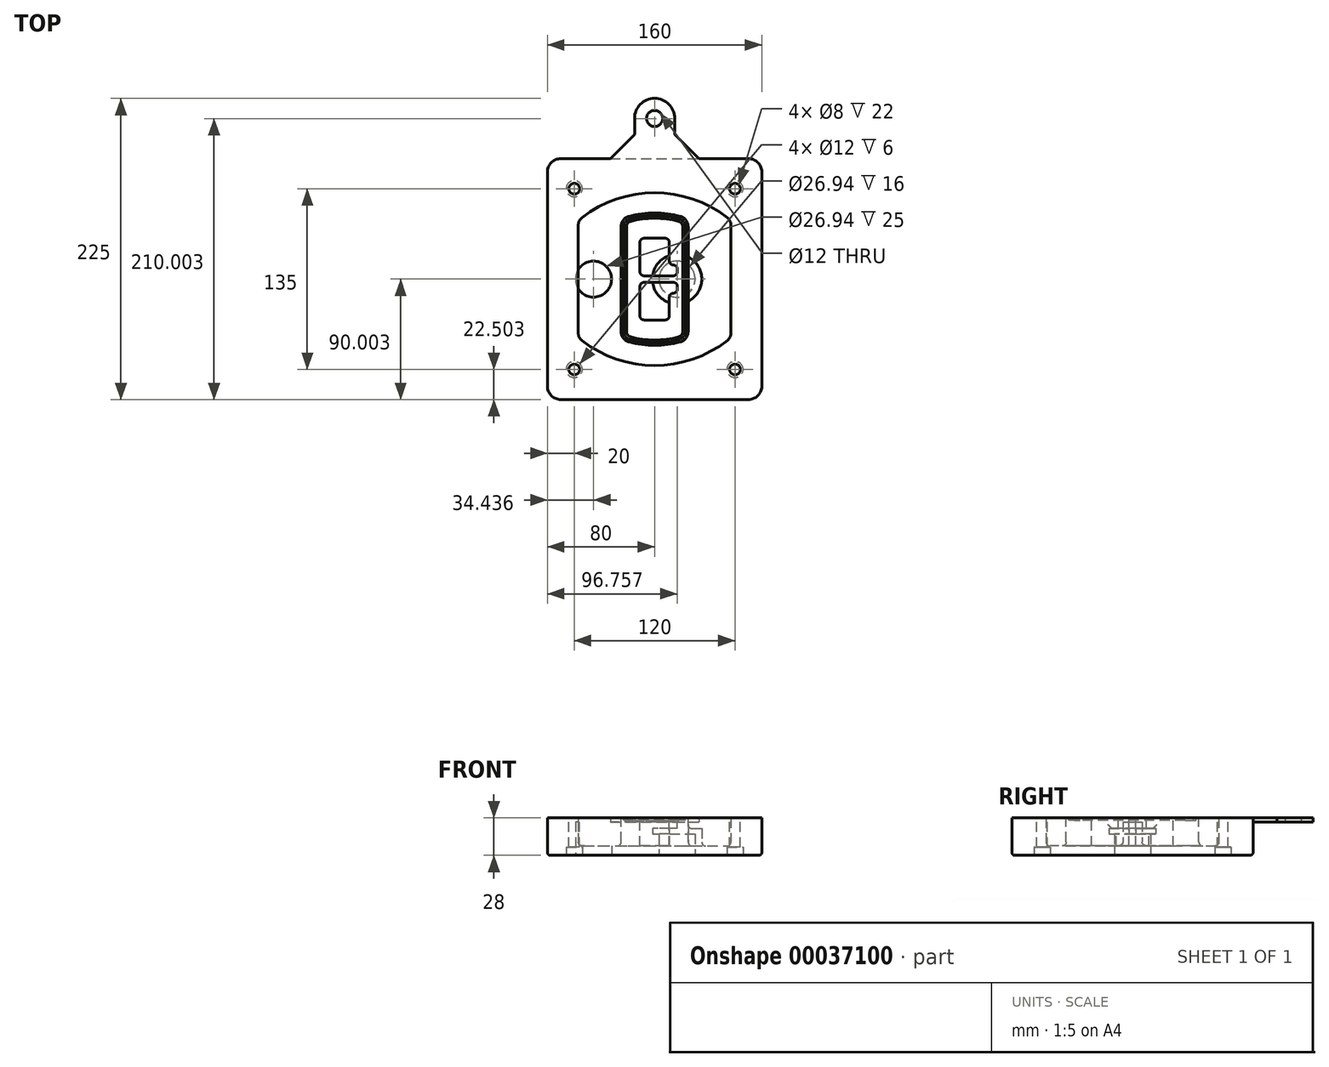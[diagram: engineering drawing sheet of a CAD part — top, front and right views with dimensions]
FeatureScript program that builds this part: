
annotation { "Feature Type Name" : "Feature", "Feature Type Description" : "" }
export const myFeature = defineFeature(function(context is Context, id is Id, definition is map)
    precondition{}
    {
        {
            var Q0;
            Q0=qCreatedBy(makeId("Top.planeOp"),FACE);
            var sketch = newSketch(context, id + "F0", { "sketchPlane" : qUnion([Q0])});
            skPoint(sketch, "E0.rect.middle", {"position": v(0, 0) * mm});
            skLineSegment(sketch, "E1.bottom", {"start": v(24.05, 28.38) * mm, "end": v(164.05, 28.38) * mm});
            skLineSegment(sketch, "E1.top", {"start": v(24.05, 208.38) * mm, "end": v(164.05, 208.38) * mm});
            skLineSegment(sketch, "E1.left", {"start": v(14.05, 38.38) * mm, "end": v(14.05, 198.38) * mm});
            skLineSegment(sketch, "E1.right", {"start": v(174.05, 38.38) * mm, "end": v(174.05, 198.38) * mm});
            skLineSegment(sketch, "E2", {"start": v(14.05, 208.38) * mm, "end": v(174.05, 28.38) * mm, "construction": true});
            skLineSegment(sketch, "E3", {"start": v(174.05, 208.38) * mm, "end": v(14.05, 28.38) * mm, "construction": true});
            skCircle(sketch, "E4", {"center": v(34.05, 185.88) * mm, "radius": 4 * mm});
            skCircle(sketch, "E5", {"center": v(154.05, 185.88) * mm, "radius": 4 * mm});
            skCircle(sketch, "E6", {"center": v(154.05, 50.88) * mm, "radius": 4 * mm});
            skCircle(sketch, "E7", {"center": v(34.05, 50.88) * mm, "radius": 4 * mm});
            skLineSegment(sketch, "E8", {"start": v(34.05, 185.88) * mm, "end": v(154.05, 185.88) * mm, "construction": true});
            skLineSegment(sketch, "E9", {"start": v(154.05, 185.88) * mm, "end": v(154.05, 50.88) * mm, "construction": true});
            skLineSegment(sketch, "E10", {"start": v(154.05, 50.88) * mm, "end": v(34.05, 50.88) * mm, "construction": true});
            skLineSegment(sketch, "E11", {"start": v(34.05, 50.88) * mm, "end": v(34.05, 185.88) * mm, "construction": true});
            skLineSegment(sketch, "E12", {"start": v(34.05, 158.68) * mm, "end": v(34.05, 78.09) * mm});
            skLineSegment(sketch, "E13", {"start": v(154.05, 158.68) * mm, "end": v(154.05, 78.09) * mm});
            skArc(sketch, "E14", {"start": v(150.2, 166.56) * mm, "mid": v(94.05, 185.88) * mm, "end": v(37.9, 166.56) * mm});
            skArc(sketch, "E15", {"start": v(37.9, 70.2) * mm, "mid": v(94.05, 50.88) * mm, "end": v(150.2, 70.2) * mm});
            skLineSegment(sketch, "E16", {"start": v(34.05, 118.38) * mm, "end": v(154.05, 118.38) * mm, "construction": true});
            skPoint(sketch, "E17.visualSharp", {"position": v(34.05, 73.38) * mm});
            skArc(sketch, "E17.filletArc", {"start": v(34.05, 78.09) * mm, "mid": v(35.06, 73.7) * mm, "end": v(37.9, 70.2) * mm});
            skPoint(sketch, "E18.visualSharp", {"position": v(34.05, 163.38) * mm});
            skArc(sketch, "E18.filletArc", {"start": v(37.9, 166.56) * mm, "mid": v(35.06, 163.06) * mm, "end": v(34.05, 158.68) * mm});
            skPoint(sketch, "E19.visualSharp", {"position": v(154.05, 163.38) * mm});
            skArc(sketch, "E19.filletArc", {"start": v(154.05, 158.68) * mm, "mid": v(153.04, 163.06) * mm, "end": v(150.2, 166.56) * mm});
            skPoint(sketch, "E20.visualSharp", {"position": v(154.05, 73.38) * mm});
            skArc(sketch, "E20.filletArc", {"start": v(150.2, 70.2) * mm, "mid": v(153.04, 73.7) * mm, "end": v(154.05, 78.09) * mm});
            skPoint(sketch, "E21.visualSharp", {"position": v(14.05, 208.38) * mm});
            skArc(sketch, "E21.filletArc", {"start": v(24.05, 208.38) * mm, "mid": v(16.98, 205.45) * mm, "end": v(14.05, 198.38) * mm});
            skPoint(sketch, "E22.visualSharp", {"position": v(174.05, 208.38) * mm});
            skArc(sketch, "E22.filletArc", {"start": v(174.05, 198.38) * mm, "mid": v(171.12, 205.45) * mm, "end": v(164.05, 208.38) * mm});
            skPoint(sketch, "E23.visualSharp", {"position": v(174.05, 28.38) * mm});
            skArc(sketch, "E23.filletArc", {"start": v(164.05, 28.38) * mm, "mid": v(171.12, 31.31) * mm, "end": v(174.05, 38.38) * mm});
            skPoint(sketch, "E24.visualSharp", {"position": v(14.05, 28.38) * mm});
            skArc(sketch, "E24.filletArc", {"start": v(14.05, 38.38) * mm, "mid": v(16.98, 31.31) * mm, "end": v(24.05, 28.38) * mm});
            skArc(sketch, "E25.0", {"start": v(151.05, 158.68) * mm, "mid": v(150.34, 161.75) * mm, "end": v(148.36, 164.2) * mm});
            skLineSegment(sketch, "E25.1", {"start": v(151.05, 158.68) * mm, "end": v(151.05, 78.09) * mm});
            skArc(sketch, "E25.2", {"start": v(148.36, 72.57) * mm, "mid": v(150.34, 75.02) * mm, "end": v(151.05, 78.09) * mm});
            skArc(sketch, "E25.3", {"start": v(39.74, 72.57) * mm, "mid": v(94.05, 53.88) * mm, "end": v(148.36, 72.57) * mm});
            skArc(sketch, "E25.4", {"start": v(37.05, 78.09) * mm, "mid": v(37.76, 75.02) * mm, "end": v(39.74, 72.57) * mm});
            skArc(sketch, "E25.5", {"start": v(148.36, 164.2) * mm, "mid": v(94.05, 182.88) * mm, "end": v(39.74, 164.2) * mm});
            skLineSegment(sketch, "E25.6", {"start": v(37.05, 158.68) * mm, "end": v(37.05, 78.09) * mm});
            skArc(sketch, "E25.7", {"start": v(39.74, 164.2) * mm, "mid": v(37.76, 161.75) * mm, "end": v(37.05, 158.68) * mm});
            skArc(sketch, "E26.0", {"start": v(35.43, 169.71) * mm, "mid": v(31.47, 164.82) * mm, "end": v(30.05, 158.68) * mm});
            skArc(sketch, "E26.1", {"start": v(152.67, 169.71) * mm, "mid": v(94.05, 189.88) * mm, "end": v(35.43, 169.71) * mm});
            skArc(sketch, "E26.2", {"start": v(158.05, 158.68) * mm, "mid": v(156.63, 164.82) * mm, "end": v(152.67, 169.71) * mm});
            skLineSegment(sketch, "E26.3", {"start": v(158.05, 158.68) * mm, "end": v(158.05, 78.09) * mm});
            skArc(sketch, "E26.4", {"start": v(152.67, 67.05) * mm, "mid": v(156.63, 71.95) * mm, "end": v(158.05, 78.09) * mm});
            skLineSegment(sketch, "E26.5", {"start": v(30.05, 158.68) * mm, "end": v(30.05, 78.09) * mm});
            skArc(sketch, "E26.6", {"start": v(35.43, 67.05) * mm, "mid": v(94.05, 46.88) * mm, "end": v(152.67, 67.05) * mm});
            skArc(sketch, "E26.7", {"start": v(30.05, 78.09) * mm, "mid": v(31.47, 71.95) * mm, "end": v(35.43, 67.05) * mm});
            skSolve(sketch);
        }
        {
            var Q0;
            Q0=makeQuery(id+"F0.imprint","IMPRINT",FACE,{"disambiguationData":[TD([[makeQuery(id+"F0.imprint","IMPRINT",EDGE,{"derivedFrom":sQuery(id+"F0.wireOp",EDGE,"E1.bottom")}),1.0]])]});
            var Q1;
            Q1=makeQuery(id+"F0.imprint","IMPRINT",FACE,{"disambiguationData":[TD([[makeQuery(id+"F0.imprint","IMPRINT",EDGE,{"derivedFrom":sQuery(id+"F0.wireOp",EDGE,"E12")}),1.0]])]});
            var Q2;
            Q2=makeQuery(id+"F0.imprint","IMPRINT",FACE,{"disambiguationData":[TD([[makeQuery(id+"F0.imprint","IMPRINT",EDGE,{"derivedFrom":sQuery(id+"F0.wireOp",EDGE,"E25.0")}),1.0]])]});
            var Q3;
            Q3=makeQuery(id+"F0.imprint","IMPRINT",FACE,{"disambiguationData":[TD([[makeQuery(id+"F0.imprint","IMPRINT",EDGE,{"derivedFrom":sQuery(id+"F0.wireOp",EDGE,"E12")}),-1.0]])]});
            extrude(context, id + "F1", {"entities" : qUnion([Q0, Q1, Q2, Q3]), "oppositeDirection" : true, "depth" : 25 * mm});
        }
        {
            var Q0;
            Q0=makeQuery(id+"F0.imprint","IMPRINT",FACE,{"disambiguationData":[TD([[makeQuery(id+"F0.imprint","IMPRINT",EDGE,{"derivedFrom":sQuery(id+"F0.wireOp",EDGE,"E12")}),1.0]])]});
            extrude(context, id + "F2", {"entities" : qUnion([Q0]), "operationType" : NewBodyOperationType.ADD, "depth" : 3 * mm});
        }
        {
            var Q0;
            Q0=makeQuery(id+"F0.imprint","IMPRINT",FACE,{"disambiguationData":[TD([[makeQuery(id+"F0.imprint","IMPRINT",EDGE,{"derivedFrom":sQuery(id+"F0.wireOp",EDGE,"E25.0")}),1.0]])]});
            extrude(context, id + "F3", {"entities" : qUnion([Q0]), "operationType" : NewBodyOperationType.REMOVE, "oppositeDirection" : true, "depth" : 18 * mm});
        }
        {
            var Q0;
            Q0=makeQuery(id+"F2.opExtrude","CAP_FACE",FACE,{"disambiguationData":[OSD([sQuery(id+"F0.wireOp",EDGE,"E12"),sQuery(id+"F0.wireOp",EDGE,"E13"),sQuery(id+"F0.wireOp",EDGE,"E14"),sQuery(id+"F0.wireOp",EDGE,"E15"),sQuery(id+"F0.wireOp",EDGE,"E17.filletArc"),sQuery(id+"F0.wireOp",EDGE,"E18.filletArc"),sQuery(id+"F0.wireOp",EDGE,"E19.filletArc"),sQuery(id+"F0.wireOp",EDGE,"E20.filletArc"),sQuery(id+"F0.wireOp",EDGE,"E25.0"),sQuery(id+"F0.wireOp",EDGE,"E25.1"),sQuery(id+"F0.wireOp",EDGE,"E25.2"),sQuery(id+"F0.wireOp",EDGE,"E25.3"),sQuery(id+"F0.wireOp",EDGE,"E25.4"),sQuery(id+"F0.wireOp",EDGE,"E25.5"),sQuery(id+"F0.wireOp",EDGE,"E25.6"),sQuery(id+"F0.wireOp",EDGE,"E25.7")])],"isStart":false});
            var sketch = newSketch(context, id + "F4", { "sketchPlane" : qUnion([Q0])});
            skArc(sketch, "E27.0", {"start": v(74.97, 71.41) * mm, "mid": v(94.05, 68.88) * mm, "end": v(113.13, 71.41) * mm});
            skArc(sketch, "E28.0", {"start": v(113.13, 165.35) * mm, "mid": v(94.05, 167.88) * mm, "end": v(74.97, 165.35) * mm});
            skLineSegment(sketch, "E29", {"start": v(69.05, 157.63) * mm, "end": v(69.05, 79.14) * mm});
            skLineSegment(sketch, "E30", {"start": v(119.05, 157.63) * mm, "end": v(119.05, 79.14) * mm});
            skLineSegment(sketch, "E31", {"start": v(69.05, 163.48) * mm, "end": v(119.05, 163.48) * mm, "construction": true});
            skLineSegment(sketch, "E32", {"start": v(69.05, 73.28) * mm, "end": v(119.05, 73.28) * mm, "construction": true});
            skPoint(sketch, "E33.visualSharp", {"position": v(69.05, 163.48) * mm});
            skArc(sketch, "E33.filletArc", {"start": v(74.97, 165.35) * mm, "mid": v(70.7, 162.5) * mm, "end": v(69.05, 157.63) * mm});
            skPoint(sketch, "E34.visualSharp", {"position": v(119.05, 163.48) * mm});
            skArc(sketch, "E34.filletArc", {"start": v(119.05, 157.63) * mm, "mid": v(117.4, 162.5) * mm, "end": v(113.13, 165.35) * mm});
            skPoint(sketch, "E35.visualSharp", {"position": v(119.05, 73.28) * mm});
            skArc(sketch, "E35.filletArc", {"start": v(113.13, 71.41) * mm, "mid": v(117.4, 74.27) * mm, "end": v(119.05, 79.14) * mm});
            skPoint(sketch, "E36.visualSharp", {"position": v(69.05, 73.28) * mm});
            skArc(sketch, "E36.filletArc", {"start": v(69.05, 79.14) * mm, "mid": v(70.7, 74.27) * mm, "end": v(74.97, 71.41) * mm});
            skArc(sketch, "E37.0", {"start": v(148.36, 164.2) * mm, "mid": v(94.05, 182.88) * mm, "end": v(39.74, 164.2) * mm});
            skArc(sketch, "E37.1", {"start": v(39.74, 164.2) * mm, "mid": v(37.76, 161.75) * mm, "end": v(37.05, 158.68) * mm});
            skLineSegment(sketch, "E37.2", {"start": v(37.05, 158.68) * mm, "end": v(37.05, 78.09) * mm});
            skArc(sketch, "E37.3", {"start": v(37.05, 78.09) * mm, "mid": v(37.76, 75.02) * mm, "end": v(39.74, 72.57) * mm});
            skArc(sketch, "E37.4", {"start": v(39.74, 72.57) * mm, "mid": v(94.05, 53.88) * mm, "end": v(148.36, 72.57) * mm});
            skArc(sketch, "E37.5", {"start": v(148.36, 72.57) * mm, "mid": v(150.34, 75.02) * mm, "end": v(151.05, 78.09) * mm});
            skLineSegment(sketch, "E37.6", {"start": v(151.05, 158.68) * mm, "end": v(151.05, 78.09) * mm});
            skArc(sketch, "E37.7", {"start": v(151.05, 158.68) * mm, "mid": v(150.34, 161.75) * mm, "end": v(148.36, 164.2) * mm});
            skLineSegment(sketch, "E38.0", {"start": v(117.05, 157.63) * mm, "end": v(117.05, 79.14) * mm});
            skArc(sketch, "E38.1", {"start": v(112.61, 73.34) * mm, "mid": v(115.81, 75.49) * mm, "end": v(117.05, 79.14) * mm});
            skArc(sketch, "E38.2", {"start": v(75.49, 73.34) * mm, "mid": v(94.05, 70.88) * mm, "end": v(112.61, 73.34) * mm});
            skArc(sketch, "E38.3", {"start": v(71.05, 79.14) * mm, "mid": v(72.29, 75.49) * mm, "end": v(75.49, 73.34) * mm});
            skLineSegment(sketch, "E38.4", {"start": v(71.05, 157.63) * mm, "end": v(71.05, 79.14) * mm});
            skArc(sketch, "E38.5", {"start": v(117.05, 157.63) * mm, "mid": v(115.81, 161.28) * mm, "end": v(112.61, 163.42) * mm});
            skArc(sketch, "E38.6", {"start": v(75.49, 163.42) * mm, "mid": v(72.29, 161.28) * mm, "end": v(71.05, 157.63) * mm});
            skArc(sketch, "E38.7", {"start": v(112.61, 163.42) * mm, "mid": v(94.05, 165.88) * mm, "end": v(75.49, 163.42) * mm});
            skArc(sketch, "E39.0", {"start": v(115.05, 157.63) * mm, "mid": v(114.23, 160.06) * mm, "end": v(112.1, 161.5) * mm});
            skLineSegment(sketch, "E39.1", {"start": v(115.05, 157.63) * mm, "end": v(115.05, 79.14) * mm});
            skArc(sketch, "E39.2", {"start": v(112.1, 75.27) * mm, "mid": v(114.23, 76.7) * mm, "end": v(115.05, 79.14) * mm});
            skArc(sketch, "E39.3", {"start": v(76, 75.27) * mm, "mid": v(94.05, 72.88) * mm, "end": v(112.1, 75.27) * mm});
            skArc(sketch, "E39.4", {"start": v(73.05, 79.14) * mm, "mid": v(73.87, 76.7) * mm, "end": v(76, 75.27) * mm});
            skArc(sketch, "E39.5", {"start": v(112.1, 161.5) * mm, "mid": v(94.05, 163.88) * mm, "end": v(76, 161.5) * mm});
            skLineSegment(sketch, "E39.6", {"start": v(73.05, 157.63) * mm, "end": v(73.05, 79.14) * mm});
            skArc(sketch, "E39.7", {"start": v(76, 161.5) * mm, "mid": v(73.87, 160.06) * mm, "end": v(73.05, 157.63) * mm});
            skLineSegment(sketch, "E40", {"start": v(69.05, 118.38) * mm, "end": v(119.05, 118.38) * mm, "construction": true});
            skLineSegment(sketch, "E41", {"start": v(83.05, 123.88) * mm, "end": v(83.05, 145.88) * mm});
            skLineSegment(sketch, "E42", {"start": v(86.05, 148.88) * mm, "end": v(102.05, 148.88) * mm});
            skLineSegment(sketch, "E43", {"start": v(105.05, 145.88) * mm, "end": v(105.05, 131.88) * mm});
            skLineSegment(sketch, "E44", {"start": v(108.05, 128.88) * mm, "end": v(108.05, 128.88) * mm});
            skLineSegment(sketch, "E45", {"start": v(111.05, 125.88) * mm, "end": v(111.05, 123.88) * mm});
            skLineSegment(sketch, "E46", {"start": v(108.05, 120.88) * mm, "end": v(86.05, 120.88) * mm});
            skPoint(sketch, "E47.visualSharp", {"position": v(83.05, 148.88) * mm});
            skArc(sketch, "E47.filletArc", {"start": v(86.05, 148.88) * mm, "mid": v(83.93, 148) * mm, "end": v(83.05, 145.88) * mm});
            skPoint(sketch, "E48.visualSharp", {"position": v(105.05, 148.88) * mm});
            skArc(sketch, "E48.filletArc", {"start": v(105.05, 145.88) * mm, "mid": v(104.17, 148) * mm, "end": v(102.05, 148.88) * mm});
            skPoint(sketch, "E49.visualSharp", {"position": v(105.05, 128.88) * mm});
            skArc(sketch, "E49.filletArc", {"start": v(105.05, 131.88) * mm, "mid": v(105.93, 129.76) * mm, "end": v(108.05, 128.88) * mm});
            skPoint(sketch, "E50.visualSharp", {"position": v(111.05, 128.88) * mm});
            skArc(sketch, "E50.filletArc", {"start": v(111.05, 125.88) * mm, "mid": v(110.17, 128) * mm, "end": v(108.05, 128.88) * mm});
            skPoint(sketch, "E51.visualSharp", {"position": v(111.05, 120.88) * mm});
            skArc(sketch, "E51.filletArc", {"start": v(108.05, 120.88) * mm, "mid": v(110.17, 121.76) * mm, "end": v(111.05, 123.88) * mm});
            skPoint(sketch, "E52.visualSharp", {"position": v(83.05, 120.88) * mm});
            skArc(sketch, "E52.filletArc", {"start": v(83.05, 123.88) * mm, "mid": v(83.93, 121.76) * mm, "end": v(86.05, 120.88) * mm});
            skLineSegment(sketch, "E53.0.MirrorCS", {"start": v(108.05, 115.88) * mm, "end": v(86.05, 115.88) * mm});
            skArc(sketch, "E54.0.MirrorCS", {"start": v(83.05, 112.88) * mm, "mid": v(83.93, 115) * mm, "end": v(86.05, 115.88) * mm});
            skLineSegment(sketch, "E55.0.MirrorCS", {"start": v(83.05, 112.88) * mm, "end": v(83.05, 90.88) * mm});
            skArc(sketch, "E56.0.MirrorCS", {"start": v(86.05, 87.88) * mm, "mid": v(83.93, 88.76) * mm, "end": v(83.05, 90.88) * mm});
            skLineSegment(sketch, "E57.0.MirrorCS", {"start": v(86.05, 87.88) * mm, "end": v(102.05, 87.88) * mm});
            skArc(sketch, "E58.0.MirrorCS", {"start": v(105.05, 90.88) * mm, "mid": v(104.17, 88.76) * mm, "end": v(102.05, 87.88) * mm});
            skLineSegment(sketch, "E59.0.MirrorCS", {"start": v(105.05, 90.88) * mm, "end": v(105.05, 104.88) * mm});
            skArc(sketch, "E60.0.MirrorCS", {"start": v(105.05, 104.88) * mm, "mid": v(105.93, 107) * mm, "end": v(108.05, 107.88) * mm});
            skArc(sketch, "E61.0.MirrorCS", {"start": v(111.05, 110.88) * mm, "mid": v(110.17, 108.76) * mm, "end": v(108.05, 107.88) * mm});
            skLineSegment(sketch, "E62.0.MirrorCS", {"start": v(111.05, 110.88) * mm, "end": v(111.05, 112.88) * mm});
            skArc(sketch, "E63.0.MirrorCS", {"start": v(108.05, 115.88) * mm, "mid": v(110.17, 115) * mm, "end": v(111.05, 112.88) * mm});
            skSolve(sketch);
        }
        {
            var Q0;
            Q0=makeQuery(id+"F4.imprint","IMPRINT",FACE,{"disambiguationData":[TD([[makeQuery(id+"F4.imprint","IMPRINT",EDGE,{"derivedFrom":sQuery(id+"F4.wireOp",EDGE,"E27.0")}),1.0]])]});
            var Q1;
            Q1=makeQuery(id+"F4.imprint","IMPRINT",FACE,{"disambiguationData":[TD([[makeQuery(id+"F4.imprint","IMPRINT",EDGE,{"derivedFrom":sQuery(id+"F4.wireOp",EDGE,"E38.0")}),-1.0]])]});
            var Q2;
            Q2=makeQuery(id+"F4.imprint","IMPRINT",FACE,{"disambiguationData":[TD([[makeQuery(id+"F4.imprint","IMPRINT",EDGE,{"derivedFrom":sQuery(id+"F4.wireOp",EDGE,"E39.0")}),1.0]])]});
            extrude(context, id + "F5", {"entities" : qUnion([Q0, Q1, Q2]), "operationType" : NewBodyOperationType.ADD, "endBound" : BoundingType.UP_TO_NEXT, "oppositeDirection" : true, "depth" : 25 * mm});
        }
        {
            var Q0;
            Q0=makeQuery(id+"F4.imprint","IMPRINT",FACE,{"disambiguationData":[TD([[makeQuery(id+"F4.imprint","IMPRINT",EDGE,{"derivedFrom":sQuery(id+"F4.wireOp",EDGE,"E38.0")}),-1.0]])]});
            extrude(context, id + "F6", {"entities" : qUnion([Q0]), "operationType" : NewBodyOperationType.REMOVE, "oppositeDirection" : true, "depth" : 2 * mm});
        }
        {
            var Q0;
            Q0=makeQuery(id+"F1.opExtrude","CAP_FACE",FACE,{"disambiguationData":[OSD([sQuery(id+"F0.wireOp",EDGE,"E1.bottom"),sQuery(id+"F0.wireOp",EDGE,"E1.top"),sQuery(id+"F0.wireOp",EDGE,"E1.left"),sQuery(id+"F0.wireOp",EDGE,"E1.right"),sQuery(id+"F0.wireOp",EDGE,"E4"),sQuery(id+"F0.wireOp",EDGE,"E5"),sQuery(id+"F0.wireOp",EDGE,"E6"),sQuery(id+"F0.wireOp",EDGE,"E7"),sQuery(id+"F0.wireOp",EDGE,"E21.filletArc"),sQuery(id+"F0.wireOp",EDGE,"E22.filletArc"),sQuery(id+"F0.wireOp",EDGE,"E23.filletArc"),sQuery(id+"F0.wireOp",EDGE,"E24.filletArc")])],"isStart":false});
            var sketch = newSketch(context, id + "F7", { "sketchPlane" : qUnion([Q0])});
            skCircle(sketch, "E64", {"center": v(110.8, -118.38) * mm, "radius": 13.47 * mm});
            skCircle(sketch, "E65", {"center": v(48.49, -118.38) * mm, "radius": 13.47 * mm});
            skLineSegment(sketch, "E66", {"start": v(174.05, -118.38) * mm, "end": v(14.05, -118.38) * mm});
            skCircle(sketch, "E67", {"center": v(110.8, -118.38) * mm, "radius": 18.47 * mm});
            skCircle(sketch, "E68", {"center": v(154.05, -185.88) * mm, "radius": 6 * mm});
            skCircle(sketch, "E69", {"center": v(34.05, -185.88) * mm, "radius": 6 * mm});
            skCircle(sketch, "E70", {"center": v(34.05, -50.88) * mm, "radius": 6 * mm});
            skCircle(sketch, "E71", {"center": v(154.05, -50.88) * mm, "radius": 6 * mm});
            skSolve(sketch);
        }
        {
            var Q0;
            {var subQ1=sQuery(id+"F7.wireOp",EDGE,"E66");var subQ4=sQuery(id+"F7.wireOp",EDGE,"E64");var subQ6=makeQuery(id+"F7.imprint","INTERSECT",VERTEX,{"disambiguationData":[OD(0.0)],"derivedFrom":[subQ4,subQ1]});Q0=makeQuery(id+"F7.imprint","IMPRINT",FACE,{"disambiguationData":[TD([[makeQuery(id+"F7.imprint","IMPRINT",EDGE,{"disambiguationData":[TD([[subQ6,-1.0]])],"derivedFrom":subQ4}),-1.0]])]});}
            var Q1;
            {var subQ0=sQuery(id+"F7.wireOp",EDGE,"E66");var subQ1=sQuery(id+"F7.wireOp",EDGE,"E64");var subQ3=makeQuery(id+"F7.imprint","INTERSECT",VERTEX,{"disambiguationData":[OD(0.0)],"derivedFrom":[subQ1,subQ0]});Q1=makeQuery(id+"F7.imprint","IMPRINT",FACE,{"disambiguationData":[TD([[makeQuery(id+"F7.imprint","IMPRINT",EDGE,{"disambiguationData":[TD([[subQ3,-1.0]])],"derivedFrom":subQ1}),1.0]])]});}
            var Q2;
            {var subQ0=sQuery(id+"F7.wireOp",EDGE,"E66");var subQ1=sQuery(id+"F7.wireOp",EDGE,"E64");var subQ3=makeQuery(id+"F7.imprint","INTERSECT",VERTEX,{"disambiguationData":[OD(0.0)],"derivedFrom":[subQ1,subQ0]});Q2=makeQuery(id+"F7.imprint","IMPRINT",FACE,{"disambiguationData":[TD([[makeQuery(id+"F7.imprint","IMPRINT",EDGE,{"disambiguationData":[TD([[subQ3,1.0]])],"derivedFrom":subQ1}),1.0]])]});}
            var Q3;
            {var subQ1=sQuery(id+"F7.wireOp",EDGE,"E66");var subQ4=sQuery(id+"F7.wireOp",EDGE,"E64");var subQ6=makeQuery(id+"F7.imprint","INTERSECT",VERTEX,{"disambiguationData":[OD(0.0)],"derivedFrom":[subQ4,subQ1]});Q3=makeQuery(id+"F7.imprint","IMPRINT",FACE,{"disambiguationData":[TD([[makeQuery(id+"F7.imprint","IMPRINT",EDGE,{"disambiguationData":[TD([[subQ6,1.0]])],"derivedFrom":subQ4}),-1.0]])]});}
            extrude(context, id + "F8", {"entities" : qUnion([Q0, Q1, Q2, Q3]), "operationType" : NewBodyOperationType.ADD, "oppositeDirection" : true, "depth" : 20 * mm});
        }
        {
            var Q0;
            {var subQ0=sQuery(id+"F7.wireOp",EDGE,"E66");var subQ1=sQuery(id+"F7.wireOp",EDGE,"E64");var subQ3=makeQuery(id+"F7.imprint","INTERSECT",VERTEX,{"disambiguationData":[OD(0.0)],"derivedFrom":[subQ1,subQ0]});Q0=makeQuery(id+"F7.imprint","IMPRINT",FACE,{"disambiguationData":[TD([[makeQuery(id+"F7.imprint","IMPRINT",EDGE,{"disambiguationData":[TD([[subQ3,-1.0]])],"derivedFrom":subQ1}),1.0]])]});}
            var Q1;
            {var subQ0=sQuery(id+"F7.wireOp",EDGE,"E66");var subQ1=sQuery(id+"F7.wireOp",EDGE,"E64");var subQ3=makeQuery(id+"F7.imprint","INTERSECT",VERTEX,{"disambiguationData":[OD(0.0)],"derivedFrom":[subQ1,subQ0]});Q1=makeQuery(id+"F7.imprint","IMPRINT",FACE,{"disambiguationData":[TD([[makeQuery(id+"F7.imprint","IMPRINT",EDGE,{"disambiguationData":[TD([[subQ3,1.0]])],"derivedFrom":subQ1}),1.0]])]});}
            extrude(context, id + "F9", {"entities" : qUnion([Q0, Q1]), "operationType" : NewBodyOperationType.REMOVE, "oppositeDirection" : true, "depth" : 16 * mm});
        }
        {
            var Q0;
            {var subQ0=sQuery(id+"F7.wireOp",EDGE,"E66");var subQ1=sQuery(id+"F7.wireOp",EDGE,"E65");var subQ3=makeQuery(id+"F7.imprint","INTERSECT",VERTEX,{"disambiguationData":[OD(0.0)],"derivedFrom":[subQ1,subQ0]});Q0=makeQuery(id+"F7.imprint","IMPRINT",FACE,{"disambiguationData":[TD([[makeQuery(id+"F7.imprint","IMPRINT",EDGE,{"disambiguationData":[TD([[subQ3,-1.0]])],"derivedFrom":subQ1}),1.0]])]});}
            var Q1;
            {var subQ0=sQuery(id+"F7.wireOp",EDGE,"E66");var subQ1=sQuery(id+"F7.wireOp",EDGE,"E65");var subQ3=makeQuery(id+"F7.imprint","INTERSECT",VERTEX,{"disambiguationData":[OD(0.0)],"derivedFrom":[subQ1,subQ0]});Q1=makeQuery(id+"F7.imprint","IMPRINT",FACE,{"disambiguationData":[TD([[makeQuery(id+"F7.imprint","IMPRINT",EDGE,{"disambiguationData":[TD([[subQ3,1.0]])],"derivedFrom":subQ1}),1.0]])]});}
            extrude(context, id + "F10", {"entities" : qUnion([Q0, Q1]), "operationType" : NewBodyOperationType.REMOVE, "oppositeDirection" : true, "depth" : 25 * mm});
        }
        {
            var Q0;
            Q0=makeQuery(id+"F7.imprint","IMPRINT",FACE,{"disambiguationData":[TD([[makeQuery(id+"F7.imprint","IMPRINT",EDGE,{"derivedFrom":sQuery(id+"F7.wireOp",EDGE,"E68")}),1.0]])]});
            var Q1;
            Q1=makeQuery(id+"F7.imprint","IMPRINT",FACE,{"disambiguationData":[TD([[makeQuery(id+"F7.imprint","IMPRINT",EDGE,{"derivedFrom":makeQuery(id+"F1.opExtrude","CAP_EDGE",EDGE,{"disambiguationData":[OSD([sQuery(id+"F0.wireOp",EDGE,"E5")])],"isStart":false})}),-1.0]])]});
            var Q2;
            Q2=makeQuery(id+"F7.imprint","IMPRINT",FACE,{"disambiguationData":[TD([[makeQuery(id+"F7.imprint","IMPRINT",EDGE,{"derivedFrom":sQuery(id+"F7.wireOp",EDGE,"E69")}),1.0]])]});
            var Q3;
            Q3=makeQuery(id+"F7.imprint","IMPRINT",FACE,{"disambiguationData":[TD([[makeQuery(id+"F7.imprint","IMPRINT",EDGE,{"derivedFrom":makeQuery(id+"F1.opExtrude","CAP_EDGE",EDGE,{"disambiguationData":[OSD([sQuery(id+"F0.wireOp",EDGE,"E4")])],"isStart":false})}),-1.0]])]});
            var Q4;
            Q4=makeQuery(id+"F7.imprint","IMPRINT",FACE,{"disambiguationData":[TD([[makeQuery(id+"F7.imprint","IMPRINT",EDGE,{"derivedFrom":sQuery(id+"F7.wireOp",EDGE,"E70")}),1.0]])]});
            var Q5;
            Q5=makeQuery(id+"F7.imprint","IMPRINT",FACE,{"disambiguationData":[TD([[makeQuery(id+"F7.imprint","IMPRINT",EDGE,{"derivedFrom":makeQuery(id+"F1.opExtrude","CAP_EDGE",EDGE,{"disambiguationData":[OSD([sQuery(id+"F0.wireOp",EDGE,"E7")])],"isStart":false})}),-1.0]])]});
            var Q6;
            Q6=makeQuery(id+"F7.imprint","IMPRINT",FACE,{"disambiguationData":[TD([[makeQuery(id+"F7.imprint","IMPRINT",EDGE,{"derivedFrom":sQuery(id+"F7.wireOp",EDGE,"E71")}),1.0]])]});
            var Q7;
            Q7=makeQuery(id+"F7.imprint","IMPRINT",FACE,{"disambiguationData":[TD([[makeQuery(id+"F7.imprint","IMPRINT",EDGE,{"derivedFrom":makeQuery(id+"F1.opExtrude","CAP_EDGE",EDGE,{"disambiguationData":[OSD([sQuery(id+"F0.wireOp",EDGE,"E6")])],"isStart":false})}),-1.0]])]});
            extrude(context, id + "F11", {"entities" : qUnion([Q0, Q1, Q2, Q3, Q4, Q5, Q6, Q7]), "operationType" : NewBodyOperationType.REMOVE, "oppositeDirection" : true, "depth" : 6 * mm});
        }
        {
            var Q0;
            Q0=makeQuery(id+"F9.boolean.opBoolean","COPY",FACE,{"derivedFrom":makeQuery(id+"F9.opExtrude","CAP_FACE",FACE,{"disambiguationData":[OSD([sQuery(id+"F7.wireOp",EDGE,"E64")])],"isStart":false})});
            var sketch = newSketch(context, id + "F12", { "sketchPlane" : qUnion([Q0])});
            skArc(sketch, "E72.0", {"start": v(105.05, -100.83) * mm, "mid": v(96.62, -106.56) * mm, "end": v(92.5, -115.88) * mm});
            skArc(sketch, "E72.1", {"start": v(92.5, -120.88) * mm, "mid": v(96.62, -130.2) * mm, "end": v(105.05, -135.93) * mm});
            skLineSegment(sketch, "E73", {"start": v(92.5, -120.88) * mm, "end": v(108.05, -120.88) * mm});
            skLineSegment(sketch, "E74.0", {"start": v(108.05, -115.88) * mm, "end": v(92.5, -115.88) * mm});
            skArc(sketch, "E74.1", {"start": v(108.05, -115.88) * mm, "mid": v(110.17, -115) * mm, "end": v(111.05, -112.88) * mm});
            skLineSegment(sketch, "E74.2", {"start": v(111.05, -110.88) * mm, "end": v(111.05, -112.88) * mm});
            skArc(sketch, "E74.3", {"start": v(111.05, -110.88) * mm, "mid": v(110.17, -108.76) * mm, "end": v(108.05, -107.88) * mm});
            skArc(sketch, "E74.4", {"start": v(105.05, -104.88) * mm, "mid": v(105.93, -107) * mm, "end": v(108.05, -107.88) * mm});
            skLineSegment(sketch, "E74.5", {"start": v(105.05, -100.83) * mm, "end": v(105.05, -104.88) * mm});
            skLineSegment(sketch, "E74.7", {"start": v(108.05, -120.88) * mm, "end": v(92.5, -120.88) * mm});
            skArc(sketch, "E74.8", {"start": v(108.05, -120.88) * mm, "mid": v(110.17, -121.76) * mm, "end": v(111.05, -123.88) * mm});
            skLineSegment(sketch, "E74.9", {"start": v(111.05, -125.88) * mm, "end": v(111.05, -123.88) * mm});
            skArc(sketch, "E74.10", {"start": v(111.05, -125.88) * mm, "mid": v(110.17, -128) * mm, "end": v(108.05, -128.88) * mm});
            skArc(sketch, "E74.11", {"start": v(105.05, -131.88) * mm, "mid": v(105.93, -129.76) * mm, "end": v(108.05, -128.88) * mm});
            skLineSegment(sketch, "E74.12", {"start": v(105.05, -135.93) * mm, "end": v(105.05, -131.88) * mm});
            skPoint(sketch, "E75.orphan", {"position": v(105.05, -145.88) * mm});
            skPoint(sketch, "E76.orphan", {"position": v(86.05, -120.88) * mm});
            skPoint(sketch, "E77.orphan", {"position": v(86.05, -115.88) * mm});
            skPoint(sketch, "E78.orphan", {"position": v(105.05, -90.88) * mm});
            skSolve(sketch);
        }
        {
            var Q0;
            {var subQ7=sQuery(id+"F12.wireOp",EDGE,"E72.0");var subQ14=sQuery(id+"F12.wireOp",EDGE,"E72.1");var subQ16=sQuery(id+"F12.wireOp",EDGE,"E74.1");var subQ18=sQuery(id+"F12.wireOp",EDGE,"E74.8");Q0=qUnion([makeQuery(id+"F12.imprint","IMPRINT",FACE,{"disambiguationData":[TD([[makeQuery(id+"F12.imprint","IMPRINT",EDGE,{"derivedFrom":subQ7}),1.0]])]}),makeQuery(id+"F12.imprint","IMPRINT",FACE,{"disambiguationData":[TD([[makeQuery(id+"F12.imprint","IMPRINT",EDGE,{"derivedFrom":subQ14}),1.0]])]}),makeQuery(id+"F12.imprint","IMPRINT",FACE,{"disambiguationData":[TD([[makeQuery(id+"F12.imprint","IMPRINT",EDGE,{"derivedFrom":subQ16}),1.0]])]}),makeQuery(id+"F12.imprint","IMPRINT",FACE,{"disambiguationData":[TD([[makeQuery(id+"F12.imprint","IMPRINT",EDGE,{"derivedFrom":subQ18}),-1.0]])]})]);}
            var Q1;
            Q1=makeQuery(id+"F5.boolean.opBoolean","SPLIT",FACE,{"disambiguationData":[TD([makeQuery(id+"F5.opExtrude","SWEPT_FACE",FACE,{"disambiguationData":[OSD([sQuery(id+"F4.wireOp",EDGE,"E41")])]})])],"derivedFrom":makeQuery(id+"F3.boolean.opBoolean","COPY",FACE,{"derivedFrom":makeQuery(id+"F3.opExtrude","CAP_FACE",FACE,{"disambiguationData":[OSD([sQuery(id+"F0.wireOp",EDGE,"E25.0"),sQuery(id+"F0.wireOp",EDGE,"E25.1"),sQuery(id+"F0.wireOp",EDGE,"E25.2"),sQuery(id+"F0.wireOp",EDGE,"E25.3"),sQuery(id+"F0.wireOp",EDGE,"E25.4"),sQuery(id+"F0.wireOp",EDGE,"E25.5"),sQuery(id+"F0.wireOp",EDGE,"E25.6"),sQuery(id+"F0.wireOp",EDGE,"E25.7")])],"isStart":false})})});
            extrude(context, id + "F13", {"entities" : qUnion([Q0]), "operationType" : NewBodyOperationType.REMOVE, "endBound" : BoundingType.UP_TO_SURFACE, "endBoundEntityFace" : qUnion([Q1]), "depth" : 25 * mm});
        }
        {
            var Q0;
            Q0=makeQuery(id+"F3.boolean.opBoolean","COPY",EDGE,{"derivedFrom":makeQuery(id+"F3.opExtrude","CAP_EDGE",EDGE,{"disambiguationData":[OSD([sQuery(id+"F0.wireOp",EDGE,"E25.6")])],"isStart":false})});
            var Q1;
            Q1=makeQuery(id+"F8.boolean.opBoolean","INTERSECT",EDGE,{"derivedFrom":[makeQuery(id+"F5.opExtrude","SWEPT_FACE",FACE,{"disambiguationData":[OSD([sQuery(id+"F4.wireOp",EDGE,"E30")])]}),makeQuery(id+"F8.opExtrude","CAP_FACE",FACE,{"disambiguationData":[OSD([sQuery(id+"F7.wireOp",EDGE,"E67")])],"isStart":false})]});
            var Q2;
            Q2=makeQuery(id+"F8.boolean.opBoolean","INTERSECT",EDGE,{"disambiguationData":[OD(1.0)],"derivedFrom":[makeQuery(id+"F5.opExtrude","SWEPT_FACE",FACE,{"disambiguationData":[OSD([sQuery(id+"F4.wireOp",EDGE,"E30")])]}),makeQuery(id+"F8.opExtrude","SWEPT_FACE",FACE,{"disambiguationData":[OSD([sQuery(id+"F7.wireOp",EDGE,"E67")])]})]});
            var Q3;
            {var subQ0=sQuery(id+"F4.wireOp",EDGE,"E30");Q3=makeQuery(id+"F8.boolean.opBoolean","SPLIT",EDGE,{"disambiguationData":[TD([makeQuery(id+"F5.opExtrude","SWEPT_FACE",FACE,{"disambiguationData":[OSD([sQuery(id+"F4.wireOp",EDGE,"E35.filletArc")])]})])],"derivedFrom":makeQuery(id+"F5.opExtrude","CAP_EDGE",EDGE,{"disambiguationData":[OSD([subQ0])],"isStart":false})});}
            var Q4;
            {var subQ0=sQuery(id+"F0.wireOp",EDGE,"E25.7");var subQ1=sQuery(id+"F0.wireOp",EDGE,"E25.1");var subQ2=sQuery(id+"F0.wireOp",EDGE,"E25.6");var subQ3=sQuery(id+"F0.wireOp",EDGE,"E25.5");var subQ4=sQuery(id+"F0.wireOp",EDGE,"E25.4");var subQ5=sQuery(id+"F0.wireOp",EDGE,"E25.0");var subQ6=sQuery(id+"F0.wireOp",EDGE,"E25.2");var subQ7=sQuery(id+"F0.wireOp",EDGE,"E25.3");Q4=makeQuery(id+"F8.boolean.opBoolean","INTERSECT",EDGE,{"derivedFrom":[makeQuery(id+"F5.boolean.opBoolean","SPLIT",FACE,{"disambiguationData":[TD([makeQuery(id+"F2.opExtrude","SWEPT_FACE",FACE,{"disambiguationData":[OSD([subQ5])]})])],"derivedFrom":makeQuery(id+"F3.boolean.opBoolean","COPY",FACE,{"derivedFrom":makeQuery(id+"F3.opExtrude","CAP_FACE",FACE,{"disambiguationData":[OSD([subQ5,subQ1,subQ6,subQ7,subQ4,subQ3,subQ2,subQ0])],"isStart":false})})}),makeQuery(id+"F8.opExtrude","SWEPT_FACE",FACE,{"disambiguationData":[OSD([sQuery(id+"F7.wireOp",EDGE,"E67")])]})]});}
            var Q5;
            Q5=makeQuery(id+"F8.boolean.opBoolean","INTERSECT",EDGE,{"disambiguationData":[OD(0.0)],"derivedFrom":[makeQuery(id+"F5.opExtrude","SWEPT_FACE",FACE,{"disambiguationData":[OSD([sQuery(id+"F4.wireOp",EDGE,"E30")])]}),makeQuery(id+"F8.opExtrude","SWEPT_FACE",FACE,{"disambiguationData":[OSD([sQuery(id+"F7.wireOp",EDGE,"E67")])]})]});
            fillet(context, id + "F14", {"entities" : qUnion([Q0, Q1, Q2, Q3, Q4, Q5]), "radius" : 3 * mm, "tangentPropagation" : true, "allowEdgeOverflow" : false});
        }
        {
            var Q0;
            Q0=makeQuery(id+"F1.opExtrude","CAP_EDGE",EDGE,{"disambiguationData":[OSD([sQuery(id+"F0.wireOp",EDGE,"E1.bottom")])],"isStart":false});
            fillet(context, id + "F15", {"entities" : qUnion([Q0]), "radius" : 2 * mm, "tangentPropagation" : true, "allowEdgeOverflow" : false});
        }
        {
            var Q0;
            {var subQ0=sQuery(id+"F0.wireOp",EDGE,"E1.bottom");var subQ1=sQuery(id+"F0.wireOp",EDGE,"E1.top");var subQ2=sQuery(id+"F0.wireOp",EDGE,"E1.left");var subQ3=sQuery(id+"F0.wireOp",EDGE,"E1.right");var subQ4=sQuery(id+"F0.wireOp",EDGE,"E4");var subQ5=sQuery(id+"F0.wireOp",EDGE,"E5");var subQ6=sQuery(id+"F0.wireOp",EDGE,"E6");var subQ7=sQuery(id+"F0.wireOp",EDGE,"E7");var subQ8=sQuery(id+"F0.wireOp",EDGE,"E21.filletArc");var subQ9=sQuery(id+"F0.wireOp",EDGE,"E22.filletArc");var subQ10=sQuery(id+"F0.wireOp",EDGE,"E23.filletArc");var subQ11=sQuery(id+"F0.wireOp",EDGE,"E24.filletArc");Q0=makeQuery(id+"F2.boolean.opBoolean","SPLIT",FACE,{"disambiguationData":[TD([makeQuery(id+"F1.opExtrude","SWEPT_FACE",FACE,{"disambiguationData":[OSD([subQ0])]})])],"derivedFrom":makeQuery(id+"F1.opExtrude","CAP_FACE",FACE,{"disambiguationData":[OSD([subQ0,subQ1,subQ2,subQ3,subQ4,subQ5,subQ6,subQ7,subQ8,subQ9,subQ10,subQ11])],"isStart":true})});}
            var sketch = newSketch(context, id + "F16", { "sketchPlane" : qUnion([Q0])});
            skLineSegment(sketch, "E79", {"start": v(94.05, 208.38) * mm, "end": v(94.05, 238.38) * mm, "construction": true});
            skArc(sketch, "E80", {"start": v(109.05, 238.38) * mm, "mid": v(94.05, 253.38) * mm, "end": v(79.05, 238.38) * mm});
            skLineSegment(sketch, "E81", {"start": v(79.05, 238.38) * mm, "end": v(79.05, 226.38) * mm});
            skLineSegment(sketch, "E82", {"start": v(109.05, 238.38) * mm, "end": v(109.05, 226.38) * mm});
            skLineSegment(sketch, "E83", {"start": v(79.05, 226.38) * mm, "end": v(61.05, 208.38) * mm});
            skLineSegment(sketch, "E84", {"start": v(109.05, 226.38) * mm, "end": v(127.05, 208.38) * mm});
            skCircle(sketch, "E85", {"center": v(94.05, 238.38) * mm, "radius": 6 * mm});
            skLineSegment(sketch, "E86", {"start": v(14.05, 118.38) * mm, "end": v(174.05, 118.38) * mm, "construction": true});
            skArc(sketch, "E87.MirrorCS", {"start": v(109.05, -1.62) * mm, "mid": v(94.05, -16.62) * mm, "end": v(79.05, -1.62) * mm});
            skCircle(sketch, "E88.MirrorC", {"center": v(94.05, -1.62) * mm, "radius": 6 * mm});
            skLineSegment(sketch, "E89.MirrorCS", {"start": v(79.05, -1.62) * mm, "end": v(79.05, 10.38) * mm});
            skLineSegment(sketch, "E90.MirrorCS", {"start": v(79.05, 10.38) * mm, "end": v(61.05, 28.38) * mm});
            skLineSegment(sketch, "E91.MirrorCS", {"start": v(109.05, 10.38) * mm, "end": v(127.05, 28.38) * mm});
            skLineSegment(sketch, "E92.MirrorCS", {"start": v(109.05, -1.62) * mm, "end": v(109.05, 10.38) * mm});
            skSolve(sketch);
        }
        {
            var Q0;
            Q0=makeQuery(id+"F16.imprint","IMPRINT",FACE,{"disambiguationData":[TD([[makeQuery(id+"F16.imprint","IMPRINT",EDGE,{"derivedFrom":sQuery(id+"F16.wireOp",EDGE,"E80")}),1.0]])]});
            var Q1;
            Q1=makeQuery(id+"F16.imprint","IMPRINT",FACE,{"disambiguationData":[TD([[makeQuery(id+"F16.imprint","IMPRINT",EDGE,{"derivedFrom":sQuery(id+"F16.wireOp",EDGE,"E87.MirrorCS")}),-1.0]])]});
            var Q2;
            Q2=makeQuery(id+"F16.imprint","IMPRINT",FACE,{"disambiguationData":[TD([[makeQuery(id+"F16.imprint","IMPRINT",EDGE,{"derivedFrom":makeQuery(id+"F1.opExtrude","CAP_EDGE",EDGE,{"disambiguationData":[OSD([sQuery(id+"F0.wireOp",EDGE,"E1.left")])],"isStart":true})}),-1.0]])]});
            var Q3;
            Q3=makeQuery(id+"F2.opExtrude","CAP_FACE",FACE,{"disambiguationData":[OSD([sQuery(id+"F0.wireOp",EDGE,"E12"),sQuery(id+"F0.wireOp",EDGE,"E13"),sQuery(id+"F0.wireOp",EDGE,"E14"),sQuery(id+"F0.wireOp",EDGE,"E15"),sQuery(id+"F0.wireOp",EDGE,"E17.filletArc"),sQuery(id+"F0.wireOp",EDGE,"E18.filletArc"),sQuery(id+"F0.wireOp",EDGE,"E19.filletArc"),sQuery(id+"F0.wireOp",EDGE,"E20.filletArc"),sQuery(id+"F0.wireOp",EDGE,"E25.0"),sQuery(id+"F0.wireOp",EDGE,"E25.1"),sQuery(id+"F0.wireOp",EDGE,"E25.2"),sQuery(id+"F0.wireOp",EDGE,"E25.3"),sQuery(id+"F0.wireOp",EDGE,"E25.4"),sQuery(id+"F0.wireOp",EDGE,"E25.5"),sQuery(id+"F0.wireOp",EDGE,"E25.6"),sQuery(id+"F0.wireOp",EDGE,"E25.7")])],"isStart":false});
            extrude(context, id + "F17", {"entities" : qUnion([Q0, Q1, Q2]), "operationType" : NewBodyOperationType.ADD, "endBound" : BoundingType.UP_TO_SURFACE, "endBoundEntityFace" : qUnion([Q3]), "depth" : 25 * mm});
        }
    });
